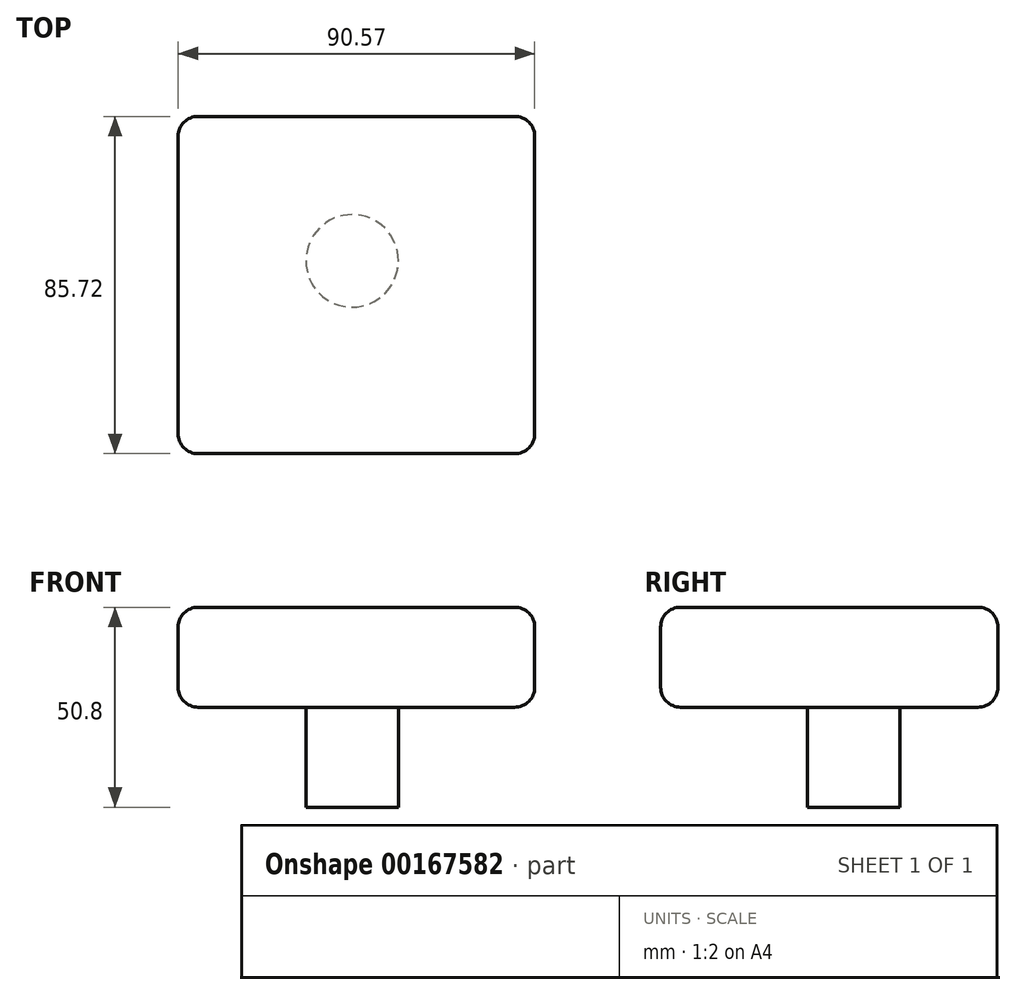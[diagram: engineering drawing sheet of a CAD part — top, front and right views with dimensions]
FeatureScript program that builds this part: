
annotation { "Feature Type Name" : "Feature", "Feature Type Description" : "" }
export const myFeature = defineFeature(function(context is Context, id is Id, definition is map)
    precondition{}
    {
        {
            var Q0;
            Q0=qCreatedBy(makeId("Top.planeOp"),FACE);
            var sketch = newSketch(context, id + "F0", { "sketchPlane" : qUnion([Q0])});
            skLineSegment(sketch, "E0.bottom", {"start": v(-44.2, 51.6) * mm, "end": v(46.38, 51.6) * mm});
            skLineSegment(sketch, "E0.top", {"start": v(-44.2, -34.12) * mm, "end": v(46.38, -34.12) * mm});
            skLineSegment(sketch, "E0.left", {"start": v(-44.2, 51.6) * mm, "end": v(-44.2, -34.12) * mm});
            skLineSegment(sketch, "E0.right", {"start": v(46.38, 51.6) * mm, "end": v(46.38, -34.12) * mm});
            skSolve(sketch);
        }
        {
            var Q0;
            Q0=makeQuery(id+"F0.imprint","IMPRINT",FACE,{"disambiguationData":[TD([[makeQuery(id+"F0.imprint","IMPRINT",EDGE,{"derivedFrom":sQuery(id+"F0.wireOp",EDGE,"E0.bottom")}),-1.0]])]});
            extrude(context, id + "F1", {"entities" : qUnion([Q0]), "depth" : 25.4 * mm});
        }
        {
            var Q0;
            Q0=makeQuery(id+"F1.opExtrude","SWEPT_FACE",FACE,{"disambiguationData":[OSD([sQuery(id+"F0.wireOp",EDGE,"E0.bottom")])]});
            var Q1;
            Q1=makeQuery(id+"F1.opExtrude","SWEPT_FACE",FACE,{"disambiguationData":[OSD([sQuery(id+"F0.wireOp",EDGE,"E0.right")])]});
            var Q2;
            Q2=makeQuery(id+"F1.opExtrude","SWEPT_FACE",FACE,{"disambiguationData":[OSD([sQuery(id+"F0.wireOp",EDGE,"E0.left")])]});
            var Q3;
            Q3=makeQuery(id+"F1.opExtrude","SWEPT_FACE",FACE,{"disambiguationData":[OSD([sQuery(id+"F0.wireOp",EDGE,"E0.top")])]});
            fillet(context, id + "F2", {"entities" : qUnion([Q0, Q1, Q2, Q3]), "radius" : 5.08 * mm, "tangentPropagation" : true, "allowEdgeOverflow" : false});
        }
        {
            var Q0;
            Q0=makeQuery(id+"F1.opExtrude","CAP_FACE",FACE,{"disambiguationData":[OSD([sQuery(id+"F0.wireOp",EDGE,"E0.bottom"),sQuery(id+"F0.wireOp",EDGE,"E0.top"),sQuery(id+"F0.wireOp",EDGE,"E0.left"),sQuery(id+"F0.wireOp",EDGE,"E0.right")])],"isStart":true});
            var sketch = newSketch(context, id + "F3", { "sketchPlane" : qUnion([Q0])});
            skCircle(sketch, "E1", {"center": v(0, -14.9) * mm, "radius": 11.74 * mm});
            skSolve(sketch);
        }
        {
            var Q0;
            Q0 = qSketchRegion(id + "F3", true);
            extrude(context, id + "F4", {"entities" : qUnion([Q0]), "operationType" : NewBodyOperationType.ADD, "depth" : 25.4 * mm});
        }
    });
